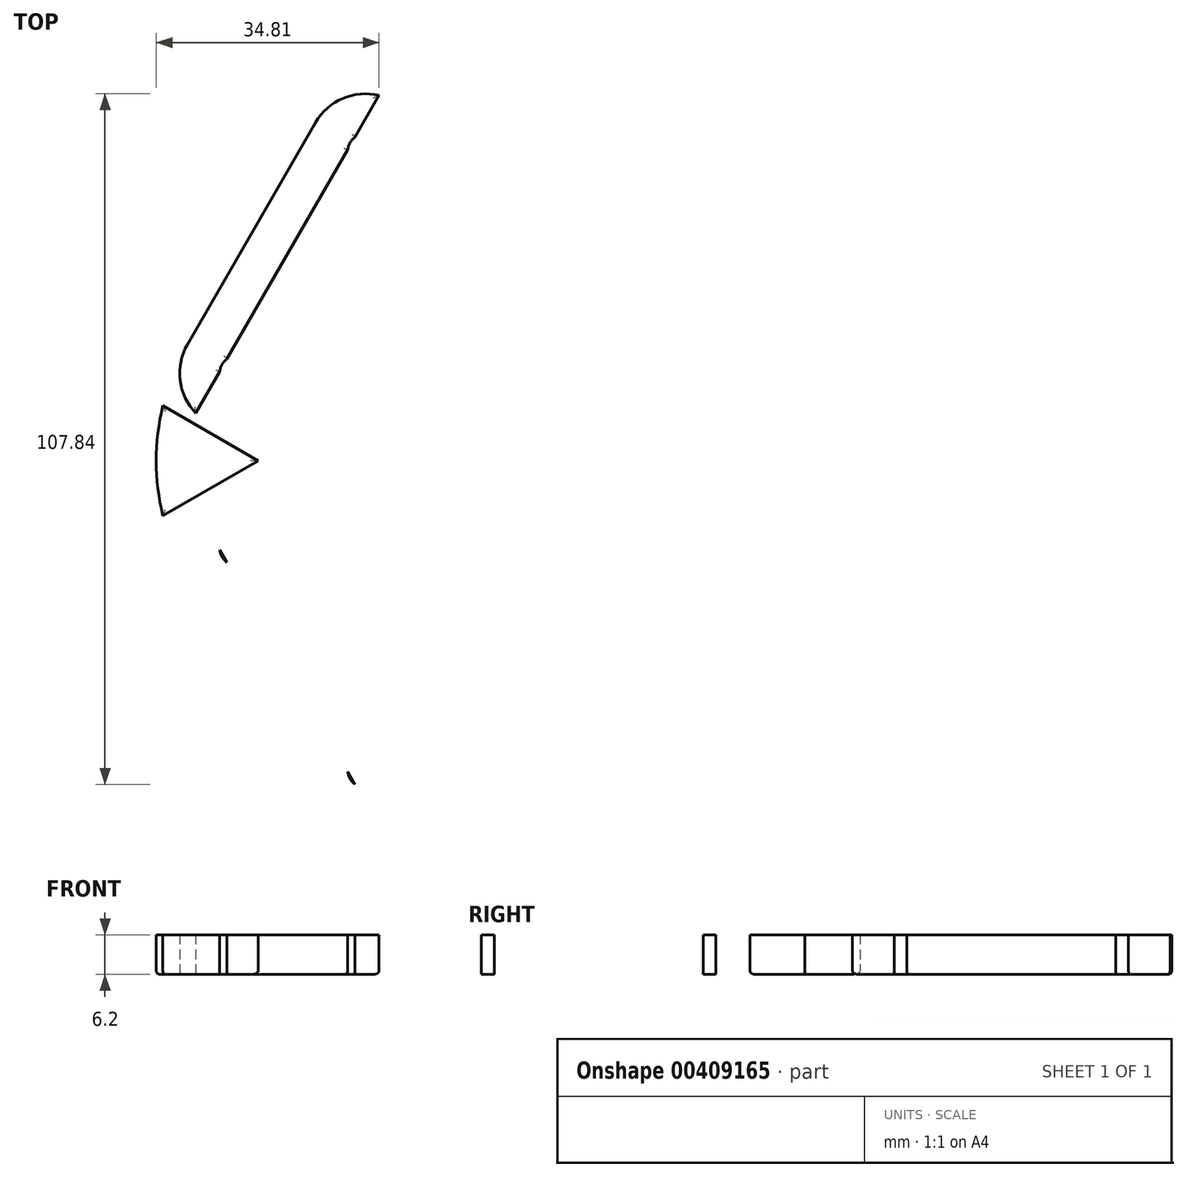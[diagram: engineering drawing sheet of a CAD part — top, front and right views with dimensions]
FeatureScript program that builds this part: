
annotation { "Feature Type Name" : "Feature", "Feature Type Description" : "" }
export const myFeature = defineFeature(function(context is Context, id is Id, definition is map)
    precondition{}
    {
        {
            var Q0;
            Q0=qCreatedBy(makeId("Top.planeOp"),FACE);
            var sketch = newSketch(context, id + "F0", { "sketchPlane" : qUnion([Q0])});
            skLineSegment(sketch, "E0", {"start": v(0, 0) * mm, "end": v(40.15, 69.55) * mm, "construction": true});
            skLineSegment(sketch, "E1", {"start": v(40.15, -69.55) * mm, "end": v(0, 0) * mm, "construction": true});
            skLineSegment(sketch, "E2", {"start": v(-5.77, 10) * mm, "end": v(11.55, 0) * mm, "construction": true});
            skCircle(sketch, "E3", {"center": v(7.89, 13.66) * mm, "radius": 10 * mm, "construction": true});
            skCircle(sketch, "E4", {"center": v(7.89, 13.66) * mm, "radius": 2.75 * mm});
            skCircle(sketch, "E5", {"center": v(17.89, 30.98) * mm, "radius": 2.75 * mm, "construction": true});
            skCircle(sketch, "E6", {"center": v(27.89, 48.3) * mm, "radius": 2.75 * mm});
            skArc(sketch, "E7", {"start": v(0.1, 18.16) * mm, "mid": v(-0.07, 9.46) * mm, "end": v(7.2, 4.69) * mm});
            skArc(sketch, "E8", {"start": v(35.68, 43.8) * mm, "mid": v(32.39, 56.1) * mm, "end": v(20.1, 52.8) * mm});
            skLineSegment(sketch, "E9", {"start": v(0.1, 18.16) * mm, "end": v(20.1, 52.8) * mm});
            skLineSegment(sketch, "E10", {"start": v(17.86, 12.94) * mm, "end": v(15.68, 9.16) * mm, "construction": true});
            skCircle(sketch, "E11.MirrorC", {"center": v(7.89, -13.66) * mm, "radius": 2.75 * mm});
            skLineSegment(sketch, "E12.MirrorCS", {"start": v(-5.77, -10) * mm, "end": v(11.55, 0) * mm, "construction": true});
            skCircle(sketch, "E13.MirrorC", {"center": v(17.89, -30.98) * mm, "radius": 2.75 * mm, "construction": true});
            skCircle(sketch, "E14.MirrorC", {"center": v(27.89, -48.3) * mm, "radius": 2.75 * mm});
            skArc(sketch, "E15.MirrorCS", {"start": v(0.1, -18.16) * mm, "mid": v(-0.07, -9.46) * mm, "end": v(7.2, -4.69) * mm});
            skCircle(sketch, "E16.MirrorC", {"center": v(7.89, -13.66) * mm, "radius": 10 * mm, "construction": true});
            skArc(sketch, "E17.MirrorCS", {"start": v(35.68, -43.8) * mm, "mid": v(32.39, -56.1) * mm, "end": v(20.1, -52.8) * mm});
            skLineSegment(sketch, "E18.MirrorCS", {"start": v(0.1, -18.16) * mm, "end": v(20.1, -52.8) * mm});
            skArc(sketch, "E19", {"start": v(7.2, 4.69) * mm, "mid": v(11.55, 0) * mm, "end": v(7.2, -4.69) * mm});
            skArc(sketch, "E20", {"start": v(35.68, 43.8) * mm, "mid": v(23.94, 0) * mm, "end": v(35.68, -43.8) * mm});
            skCircle(sketch, "E21", {"center": v(17.89, 30.98) * mm, "radius": 2.5 * mm, "construction": true});
            skLineSegment(sketch, "E22", {"start": v(34.37, 54.54) * mm, "end": v(5.73, 4.92) * mm});
            skLineSegment(sketch, "E23.MirrorCS", {"start": v(30.04, 57.04) * mm, "end": v(1.4, 7.42) * mm});
            skLineSegment(sketch, "E24.MirrorCS", {"start": v(30.04, -57.04) * mm, "end": v(1.4, -7.42) * mm});
            skLineSegment(sketch, "E25.MirrorCS", {"start": v(34.37, -54.54) * mm, "end": v(5.73, -4.92) * mm});
            skArc(sketch, "E26", {"start": v(0.1, 18.16) * mm, "mid": v(-4.77, 0) * mm, "end": v(0.1, -18.16) * mm});
            skCircle(sketch, "E27", {"center": v(0, 0) * mm, "radius": 2.75 * mm, "construction": true});
            skLineSegment(sketch, "E28", {"start": v(11.55, 0) * mm, "end": v(-4.77, 0) * mm, "construction": true});
            skLineSegment(sketch, "E29", {"start": v(11.15, 0) * mm, "end": v(-3.74, -8.6) * mm});
            skLineSegment(sketch, "E30.MirrorCS", {"start": v(11.15, 0) * mm, "end": v(-3.74, 8.6) * mm});
            skSolve(sketch);
        }
        {
            var Q0;
            {var subQ4=sQuery(id+"F0.wireOp",EDGE,"E19");Q0=makeQuery(id+"F0.imprint","IMPRINT",FACE,{"disambiguationData":[TD([[makeQuery(id+"F0.imprint","IMPRINT",EDGE,{"derivedFrom":subQ4}),1.0]])]});}
            var Q1;
            {var subQ0=sQuery(id+"F0.wireOp",EDGE,"E9");Q1=makeQuery(id+"F0.imprint","IMPRINT",FACE,{"disambiguationData":[TD([[makeQuery(id+"F0.imprint","IMPRINT",EDGE,{"derivedFrom":subQ0}),-1.0]])]});}
            var Q2;
            {var subQ0=sQuery(id+"F0.wireOp",EDGE,"E23.MirrorCS");var subQ1=sQuery(id+"F0.wireOp",EDGE,"E5");var subQ2=makeQuery(id+"F0.imprint","INTERSECT",VERTEX,{"disambiguationData":[OD(1.0)],"derivedFrom":[subQ1,subQ0]});Q2=makeQuery(id+"F0.imprint","IMPRINT",FACE,{"disambiguationData":[TD([[makeQuery(id+"F0.imprint","IMPRINT",EDGE,{"disambiguationData":[TD([[subQ2,1.0]])],"derivedFrom":subQ1}),-1.0]])]});}
            var Q3;
            {var subQ0=sQuery(id+"F0.wireOp",EDGE,"E23.MirrorCS");var subQ1=sQuery(id+"F0.wireOp",EDGE,"E6");var subQ2=makeQuery(id+"F0.imprint","INTERSECT",VERTEX,{"disambiguationData":[OD(1.0)],"derivedFrom":[subQ1,subQ0]});Q3=makeQuery(id+"F0.imprint","IMPRINT",FACE,{"disambiguationData":[TD([[makeQuery(id+"F0.imprint","IMPRINT",EDGE,{"disambiguationData":[TD([[subQ2,1.0]])],"derivedFrom":subQ1}),-1.0]])]});}
            var Q4;
            {var subQ0=sQuery(id+"F0.wireOp",EDGE,"E23.MirrorCS");var subQ1=sQuery(id+"F0.wireOp",EDGE,"E4");var subQ2=makeQuery(id+"F0.imprint","INTERSECT",VERTEX,{"disambiguationData":[OD(1.0)],"derivedFrom":[subQ1,subQ0]});Q4=makeQuery(id+"F0.imprint","IMPRINT",FACE,{"disambiguationData":[TD([[makeQuery(id+"F0.imprint","IMPRINT",EDGE,{"disambiguationData":[TD([[subQ2,1.0]])],"derivedFrom":subQ1}),-1.0]])]});}
            var Q5;
            {var subQ0=sQuery(id+"F0.wireOp",EDGE,"E23.MirrorCS");var subQ1=sQuery(id+"F0.wireOp",EDGE,"E4");var subQ2=makeQuery(id+"F0.imprint","INTERSECT",VERTEX,{"disambiguationData":[OD(0.0)],"derivedFrom":[subQ1,subQ0]});Q5=makeQuery(id+"F0.imprint","IMPRINT",FACE,{"disambiguationData":[TD([[makeQuery(id+"F0.imprint","IMPRINT",EDGE,{"disambiguationData":[TD([[subQ2,-1.0]])],"derivedFrom":subQ1}),-1.0]])]});}
            var Q6;
            {var subQ0=sQuery(id+"F0.wireOp",EDGE,"E24.MirrorCS");var subQ1=sQuery(id+"F0.wireOp",EDGE,"E11.MirrorC");var subQ2=makeQuery(id+"F0.imprint","INTERSECT",VERTEX,{"disambiguationData":[OD(0.0)],"derivedFrom":[subQ1,subQ0]});Q6=makeQuery(id+"F0.imprint","IMPRINT",FACE,{"disambiguationData":[TD([[makeQuery(id+"F0.imprint","IMPRINT",EDGE,{"disambiguationData":[TD([[subQ2,-1.0]])],"derivedFrom":subQ1}),1.0]])]});}
            var Q7;
            {var subQ0=sQuery(id+"F0.wireOp",EDGE,"E24.MirrorCS");var subQ1=sQuery(id+"F0.wireOp",EDGE,"E11.MirrorC");var subQ2=makeQuery(id+"F0.imprint","INTERSECT",VERTEX,{"disambiguationData":[OD(1.0)],"derivedFrom":[subQ1,subQ0]});Q7=makeQuery(id+"F0.imprint","IMPRINT",FACE,{"disambiguationData":[TD([[makeQuery(id+"F0.imprint","IMPRINT",EDGE,{"disambiguationData":[TD([[subQ2,1.0]])],"derivedFrom":subQ1}),1.0]])]});}
            var Q8;
            {var subQ0=sQuery(id+"F0.wireOp",EDGE,"E24.MirrorCS");var subQ1=sQuery(id+"F0.wireOp",EDGE,"E13.MirrorC");var subQ2=makeQuery(id+"F0.imprint","INTERSECT",VERTEX,{"disambiguationData":[OD(1.0)],"derivedFrom":[subQ1,subQ0]});Q8=makeQuery(id+"F0.imprint","IMPRINT",FACE,{"disambiguationData":[TD([[makeQuery(id+"F0.imprint","IMPRINT",EDGE,{"disambiguationData":[TD([[subQ2,1.0]])],"derivedFrom":subQ1}),1.0]])]});}
            var Q9;
            {var subQ0=sQuery(id+"F0.wireOp",EDGE,"E24.MirrorCS");var subQ1=sQuery(id+"F0.wireOp",EDGE,"E14.MirrorC");var subQ2=makeQuery(id+"F0.imprint","INTERSECT",VERTEX,{"disambiguationData":[OD(1.0)],"derivedFrom":[subQ1,subQ0]});Q9=makeQuery(id+"F0.imprint","IMPRINT",FACE,{"disambiguationData":[TD([[makeQuery(id+"F0.imprint","IMPRINT",EDGE,{"disambiguationData":[TD([[subQ2,1.0]])],"derivedFrom":subQ1}),1.0]])]});}
            var Q10;
            {var subQ0=sQuery(id+"F0.wireOp",EDGE,"E18.MirrorCS");Q10=makeQuery(id+"F0.imprint","IMPRINT",FACE,{"disambiguationData":[TD([[makeQuery(id+"F0.imprint","IMPRINT",EDGE,{"derivedFrom":subQ0}),1.0]])]});}
            var Q11;
            {var subQ3=sQuery(id+"F0.wireOp",EDGE,"E19");Q11=makeQuery(id+"F0.imprint","IMPRINT",FACE,{"disambiguationData":[TD([[makeQuery(id+"F0.imprint","IMPRINT",EDGE,{"derivedFrom":subQ3}),-1.0]])]});}
            var Q12;
            {var subQ1=sQuery(id+"F0.wireOp",EDGE,"E2");var subQ3=sQuery(id+"F0.wireOp",EDGE,"E26");var subQ4=makeQuery(id+"F0.imprint","INTERSECT",VERTEX,{"derivedFrom":[subQ1,subQ3]});Q12=makeQuery(id+"F0.imprint","IMPRINT",FACE,{"disambiguationData":[TD([[makeQuery(id+"F0.imprint","IMPRINT",EDGE,{"disambiguationData":[TD([[subQ4,-1.0]])],"derivedFrom":subQ3}),1.0]])]});}
            extrude(context, id + "F1", {"entities" : qUnion([Q0, Q1, Q2, Q3, Q4, Q5, Q6, Q7, Q8, Q9, Q10, Q11, Q12]), "depth" : 5 * mm, "offsetDistance" : 25 * mm});
        }
        {
            var Q0;
            {var subQ0=sQuery(id+"F0.wireOp",EDGE,"E23.MirrorCS");var subQ1=sQuery(id+"F0.wireOp",EDGE,"E6");var subQ2=makeQuery(id+"F0.imprint","INTERSECT",VERTEX,{"disambiguationData":[OD(1.0)],"derivedFrom":[subQ1,subQ0]});Q0=makeQuery(id+"F0.imprint","IMPRINT",FACE,{"disambiguationData":[TD([[makeQuery(id+"F0.imprint","IMPRINT",EDGE,{"disambiguationData":[TD([[subQ2,1.0]])],"derivedFrom":subQ1}),-1.0]])]});}
            var Q1;
            {var subQ0=sQuery(id+"F0.wireOp",EDGE,"E23.MirrorCS");var subQ1=sQuery(id+"F0.wireOp",EDGE,"E5");var subQ2=makeQuery(id+"F0.imprint","INTERSECT",VERTEX,{"disambiguationData":[OD(1.0)],"derivedFrom":[subQ1,subQ0]});Q1=makeQuery(id+"F0.imprint","IMPRINT",FACE,{"disambiguationData":[TD([[makeQuery(id+"F0.imprint","IMPRINT",EDGE,{"disambiguationData":[TD([[subQ2,1.0]])],"derivedFrom":subQ1}),-1.0]])]});}
            var Q2;
            {var subQ0=sQuery(id+"F0.wireOp",EDGE,"E23.MirrorCS");var subQ1=sQuery(id+"F0.wireOp",EDGE,"E4");var subQ2=makeQuery(id+"F0.imprint","INTERSECT",VERTEX,{"disambiguationData":[OD(1.0)],"derivedFrom":[subQ1,subQ0]});Q2=makeQuery(id+"F0.imprint","IMPRINT",FACE,{"disambiguationData":[TD([[makeQuery(id+"F0.imprint","IMPRINT",EDGE,{"disambiguationData":[TD([[subQ2,1.0]])],"derivedFrom":subQ1}),-1.0]])]});}
            var Q3;
            {var subQ0=sQuery(id+"F0.wireOp",EDGE,"E23.MirrorCS");var subQ1=sQuery(id+"F0.wireOp",EDGE,"E4");var subQ2=makeQuery(id+"F0.imprint","INTERSECT",VERTEX,{"disambiguationData":[OD(0.0)],"derivedFrom":[subQ1,subQ0]});Q3=makeQuery(id+"F0.imprint","IMPRINT",FACE,{"disambiguationData":[TD([[makeQuery(id+"F0.imprint","IMPRINT",EDGE,{"disambiguationData":[TD([[subQ2,-1.0]])],"derivedFrom":subQ1}),-1.0]])]});}
            var Q4;
            {var subQ0=sQuery(id+"F0.wireOp",EDGE,"E24.MirrorCS");var subQ1=sQuery(id+"F0.wireOp",EDGE,"E11.MirrorC");var subQ2=makeQuery(id+"F0.imprint","INTERSECT",VERTEX,{"disambiguationData":[OD(0.0)],"derivedFrom":[subQ1,subQ0]});Q4=makeQuery(id+"F0.imprint","IMPRINT",FACE,{"disambiguationData":[TD([[makeQuery(id+"F0.imprint","IMPRINT",EDGE,{"disambiguationData":[TD([[subQ2,-1.0]])],"derivedFrom":subQ1}),1.0]])]});}
            var Q5;
            {var subQ0=sQuery(id+"F0.wireOp",EDGE,"E24.MirrorCS");var subQ1=sQuery(id+"F0.wireOp",EDGE,"E11.MirrorC");var subQ2=makeQuery(id+"F0.imprint","INTERSECT",VERTEX,{"disambiguationData":[OD(1.0)],"derivedFrom":[subQ1,subQ0]});Q5=makeQuery(id+"F0.imprint","IMPRINT",FACE,{"disambiguationData":[TD([[makeQuery(id+"F0.imprint","IMPRINT",EDGE,{"disambiguationData":[TD([[subQ2,1.0]])],"derivedFrom":subQ1}),1.0]])]});}
            var Q6;
            {var subQ0=sQuery(id+"F0.wireOp",EDGE,"E24.MirrorCS");var subQ1=sQuery(id+"F0.wireOp",EDGE,"E13.MirrorC");var subQ2=makeQuery(id+"F0.imprint","INTERSECT",VERTEX,{"disambiguationData":[OD(1.0)],"derivedFrom":[subQ1,subQ0]});Q6=makeQuery(id+"F0.imprint","IMPRINT",FACE,{"disambiguationData":[TD([[makeQuery(id+"F0.imprint","IMPRINT",EDGE,{"disambiguationData":[TD([[subQ2,1.0]])],"derivedFrom":subQ1}),1.0]])]});}
            var Q7;
            {var subQ0=sQuery(id+"F0.wireOp",EDGE,"E24.MirrorCS");var subQ1=sQuery(id+"F0.wireOp",EDGE,"E14.MirrorC");var subQ2=makeQuery(id+"F0.imprint","INTERSECT",VERTEX,{"disambiguationData":[OD(1.0)],"derivedFrom":[subQ1,subQ0]});Q7=makeQuery(id+"F0.imprint","IMPRINT",FACE,{"disambiguationData":[TD([[makeQuery(id+"F0.imprint","IMPRINT",EDGE,{"disambiguationData":[TD([[subQ2,1.0]])],"derivedFrom":subQ1}),1.0]])]});}
            var Q8;
            {var subQ1=sQuery(id+"F0.wireOp",EDGE,"E2");var subQ3=sQuery(id+"F0.wireOp",EDGE,"E26");var subQ4=makeQuery(id+"F0.imprint","INTERSECT",VERTEX,{"derivedFrom":[subQ1,subQ3]});Q8=makeQuery(id+"F0.imprint","IMPRINT",FACE,{"disambiguationData":[TD([[makeQuery(id+"F0.imprint","IMPRINT",EDGE,{"disambiguationData":[TD([[subQ4,-1.0]])],"derivedFrom":subQ3}),1.0]])]});}
            extrude(context, id + "F2", {"entities" : qUnion([Q0, Q1, Q2, Q3, Q4, Q5, Q6, Q7, Q8]), "operationType" : NewBodyOperationType.ADD, "oppositeDirection" : true, "depth" : 1.2 * mm, "offsetDistance" : 25 * mm});
        }
        {
            var Q0;
            Q0=makeQuery(id+"F2.opExtrude","CAP_FACE",FACE,{"disambiguationData":[OSD([sQuery(id+"F0.wireOp",EDGE,"E5"),sQuery(id+"F0.wireOp",EDGE,"E6"),sQuery(id+"F0.wireOp",EDGE,"E22"),sQuery(id+"F0.wireOp",EDGE,"E23.MirrorCS")])],"isStart":false});
            var Q1;
            Q1=makeQuery(id+"F2.opExtrude","CAP_FACE",FACE,{"disambiguationData":[OSD([sQuery(id+"F0.wireOp",EDGE,"E6"),sQuery(id+"F0.wireOp",EDGE,"E8"),sQuery(id+"F0.wireOp",EDGE,"E22"),sQuery(id+"F0.wireOp",EDGE,"E23.MirrorCS")])],"isStart":false});
            var Q2;
            Q2=makeQuery(id+"F2.opExtrude","CAP_FACE",FACE,{"disambiguationData":[OSD([sQuery(id+"F0.wireOp",EDGE,"E4"),sQuery(id+"F0.wireOp",EDGE,"E5"),sQuery(id+"F0.wireOp",EDGE,"E22"),sQuery(id+"F0.wireOp",EDGE,"E23.MirrorCS")])],"isStart":false});
            var Q3;
            Q3=makeQuery(id+"F2.opExtrude","CAP_FACE",FACE,{"disambiguationData":[OSD([sQuery(id+"F0.wireOp",EDGE,"E4"),sQuery(id+"F0.wireOp",EDGE,"E7"),sQuery(id+"F0.wireOp",EDGE,"E22"),sQuery(id+"F0.wireOp",EDGE,"E23.MirrorCS")])],"isStart":false});
            var Q4;
            Q4=makeQuery(id+"F2.opExtrude","CAP_FACE",FACE,{"disambiguationData":[OSD([sQuery(id+"F0.wireOp",EDGE,"E11.MirrorC"),sQuery(id+"F0.wireOp",EDGE,"E15.MirrorCS"),sQuery(id+"F0.wireOp",EDGE,"E24.MirrorCS"),sQuery(id+"F0.wireOp",EDGE,"E25.MirrorCS")])],"isStart":false});
            var Q5;
            Q5=makeQuery(id+"F2.opExtrude","CAP_FACE",FACE,{"disambiguationData":[OSD([sQuery(id+"F0.wireOp",EDGE,"E11.MirrorC"),sQuery(id+"F0.wireOp",EDGE,"E13.MirrorC"),sQuery(id+"F0.wireOp",EDGE,"E24.MirrorCS"),sQuery(id+"F0.wireOp",EDGE,"E25.MirrorCS")])],"isStart":false});
            var Q6;
            Q6=makeQuery(id+"F2.opExtrude","CAP_FACE",FACE,{"disambiguationData":[OSD([sQuery(id+"F0.wireOp",EDGE,"E14.MirrorC"),sQuery(id+"F0.wireOp",EDGE,"E17.MirrorCS"),sQuery(id+"F0.wireOp",EDGE,"E24.MirrorCS"),sQuery(id+"F0.wireOp",EDGE,"E25.MirrorCS")])],"isStart":false});
            var Q7;
            Q7=makeQuery(id+"F2.opExtrude","CAP_FACE",FACE,{"disambiguationData":[OSD([sQuery(id+"F0.wireOp",EDGE,"E13.MirrorC"),sQuery(id+"F0.wireOp",EDGE,"E14.MirrorC"),sQuery(id+"F0.wireOp",EDGE,"E24.MirrorCS"),sQuery(id+"F0.wireOp",EDGE,"E25.MirrorCS")])],"isStart":false});
            var Q8;
            Q8=makeQuery(id+"F2.opExtrude","CAP_FACE",FACE,{"disambiguationData":[OSD([sQuery(id+"F0.wireOp",EDGE,"E2"),sQuery(id+"F0.wireOp",EDGE,"AwdjGCNM-xevV-rkCu-k57T-VdCHvtGFgJDu"),sQuery(id+"F0.wireOp",EDGE,"E26")])],"isStart":false});
            fillet(context, id + "F3", {"entities" : qUnion([Q0, Q1, Q2, Q3, Q4, Q5, Q6, Q7, Q8]), "radius" : 0.6 * mm, "tangentPropagation" : true, "allowEdgeOverflow" : false});
        }
    });
